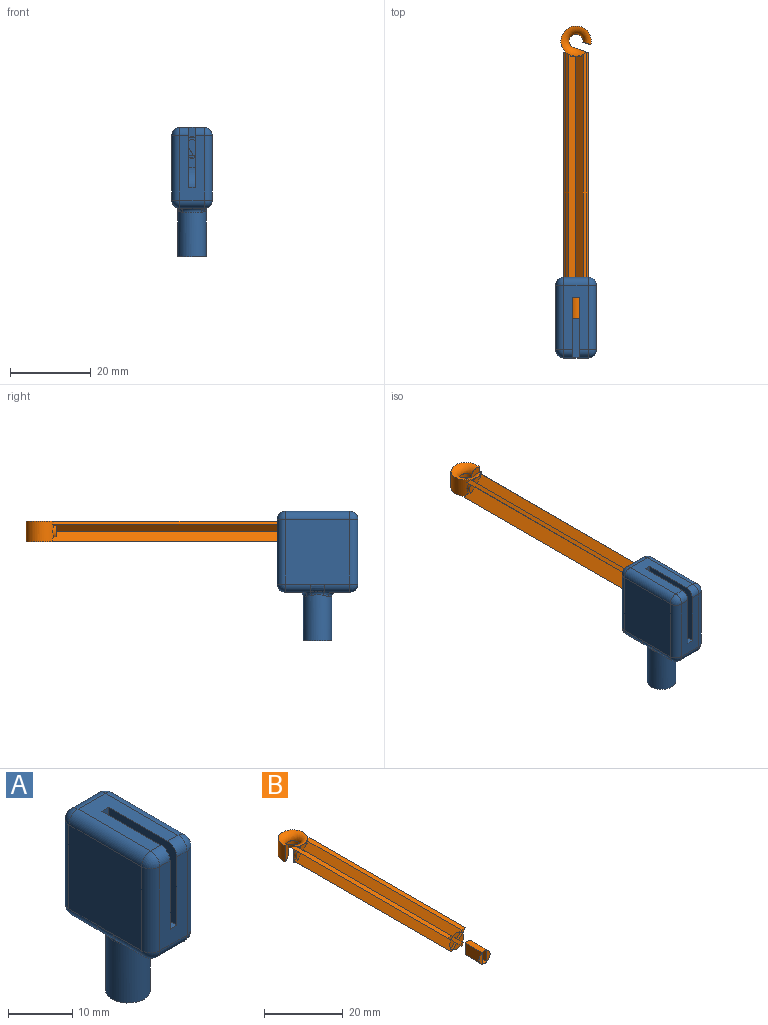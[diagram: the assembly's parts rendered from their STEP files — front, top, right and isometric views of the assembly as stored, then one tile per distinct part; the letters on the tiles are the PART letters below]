
ASSEMBLY  parts=2 mates=1
PART A: 59 faces, bbox 10x33.4x32 mm
  f0: plane 6x4.65mm, normal (0,0,-1), area 23.2mm2, adj f10,f32,f42,f48
  f1: plane 2.34x1.5mm, normal (0,-1,0), area 3.4mm2, adj f15,f16,f17,f56
  f2: cylinder r=2mm len=2.25mm, axis (1,0,0), area 7.1mm2, adj f5,f7,f17,f23
  f3: plane 16x6mm, normal (0,1,0), area 76.4mm2, adj f4,f10,f20,f28,f38
  f4: cylinder r=2mm len=6mm, axis (1,0,0), area 18.8mm2, adj f3,f5,f26,f36
  f5: plane 16x6mm, normal (0,0,1), area 76.5mm2, adj f2,f4,f6,f14,f16,f17,f24,f34
  f6: cylinder r=2mm len=2.25mm, axis (1,0,0), area 7.1mm2, adj f5,f7,f16,f33
  f7: plane 16x6mm, normal (0,-1,0), area 76.5mm2, adj f2,f6,f8,f13,f16,f17,f25,f35
  f8: cylinder r=2mm len=6mm, axis (1,0,0), area 18.8mm2, adj f7,f9,f27,f37
  f9: plane 6x4.65mm, normal (0,0,-1), area 23.2mm2, adj f8,f29,f39,f45
  f10: cylinder r=2mm len=6mm, axis (1,0,0), area 18.8mm2, adj f0,f3,f30,f40
  f11: plane 16.06x16mm, normal (-1,0,0), area 256.1mm2, adj f34,f35,f38,f39,f41,f42
  f12: plane 16.06x16mm, normal (1,0,0), area 256.1mm2, adj f24,f25,f28,f29,f31,f32
  f13: plane 10x1.5mm, normal (0,0,1), area 15mm2, adj f7,f15,f16,f17
  f14: plane 2.34x1.5mm, normal (0,-1,0), area 3.4mm2, adj f5,f16,f17,f53
  f15: cylinder r=5mm len=5mm, axis (1,0,0), area 11.8mm2, adj f1,f13,f16,f17
  f16: plane 15.05x15mm, normal (1,0,0), area 193.8mm2, adj f1,f5,f6,f7,f13,f14,f15,f53
  f17: plane 15.05x15mm, normal (-1,0,0), area 193.8mm2, adj f1,f2,f5,f7,f13,f14,f15,f51
  f18: cylinder r=3.5mm len=11.22mm, axis (0,0,1), area 243.8mm2, adj f19,f43,f44,f45,f46,f47,f48,f49
  f19: plane 7x7mm, normal (0,0,-1), area 38.5mm2, adj f18
  f20: cone r=2.5mm half-angle=3deg, axis (0,1,0), area 184.5mm2, adj f3,f21,f22,f51,f52,f53,f54,f55
  f21: plane 3.06x0.73mm, normal (0,1,0), area 1.5mm2, adj f20,f57
  f22: plane 3.06x0.73mm, normal (0,1,0), area 1.5mm2, adj f20,f52
  f23: sphere r=2mm, area 6.3mm2, adj f2,f24,f25
  f24: cylinder r=2mm len=16mm, axis (0,-1,0), area 50.3mm2, adj f5,f12,f23,f26
  f25: cylinder r=2mm len=16mm, axis (0,0,-1), area 50.3mm2, adj f7,f12,f23,f27
  f26: sphere r=2mm, area 6.3mm2, adj f4,f24,f28
  f27: sphere r=2mm, area 6.3mm2, adj f8,f25,f29
  f28: cylinder r=2mm len=16mm, axis (0,0,1), area 50.3mm2, adj f3,f12,f26,f30
  f29: cylinder r=2mm len=6.2mm, axis (0,1,0), area 18.9mm2, adj f9,f12,f27,f31,f47
  f30: sphere r=2mm, area 6.3mm2, adj f10,f28,f32
  f31: bspline ~5.28x2.45mm, area 7.6mm2, adj f12,f29,f32,f49
  f32: cylinder r=2mm len=6.2mm, axis (0,1,0), area 18.9mm2, adj f0,f12,f30,f31,f50
  f33: sphere r=2mm, area 6.3mm2, adj f6,f34,f35
  f34: cylinder r=2mm len=16mm, axis (0,1,0), area 50.3mm2, adj f5,f11,f33,f36
  f35: cylinder r=2mm len=16mm, axis (0,0,1), area 50.3mm2, adj f7,f11,f33,f37
  f36: sphere r=2mm, area 8.6mm2, adj f4,f34,f38
  f37: sphere r=2mm, area 8.6mm2, adj f8,f35,f39
  f38: cylinder r=2mm len=16mm, axis (0,0,-1), area 50.3mm2, adj f3,f11,f36,f40
  f39: cylinder r=2mm len=6.2mm, axis (0,-1,0), area 18.9mm2, adj f9,f11,f37,f41,f43
  f40: sphere r=2mm, area 4mm2, adj f10,f38,f42
  f41: bspline ~5.28x2.45mm, area 7.6mm2, adj f11,f39,f42,f44
  f42: cylinder r=2mm len=6.2mm, axis (0,-1,0), area 18.9mm2, adj f0,f11,f40,f41,f46
  f43: bspline ~3.1x2.02mm, area 2.2mm2, adj f18,f39,f44,f45
  f44: bspline ~3.88x1.01mm, area 3.5mm2, adj f18,f41,f43,f46
  f45: torus R=4.5mm, axis (0,0,1), area 8.9mm2, adj f9,f18,f43,f47
  f46: bspline ~3.1x2.02mm, area 2.2mm2, adj f18,f42,f44,f48
  f47: bspline ~3.1x2.02mm, area 2.2mm2, adj f18,f29,f45,f49
  f48: torus R=4.5mm, axis (0,0,1), area 8.9mm2, adj f0,f18,f46,f50
  f49: bspline ~3.88x1.01mm, area 3.5mm2, adj f18,f31,f47,f50
  f50: bspline ~2.54x1.89mm, area 2.2mm2, adj f18,f32,f48,f49
  f51: bspline ~25.82x1.92mm, area 3mm2, adj f17,f20,f52,f53
  f52: cylinder r=0.5mm len=4.22mm, axis (0,0,-1), area 2.8mm2, adj f17,f20,f22,f51,f54
  f53: torus R=2.76mm, axis (0,1,0), area 1.4mm2, adj f14,f16,f17,f20,f51,f55
  f54: bspline ~25.82x1.92mm, area 3mm2, adj f17,f20,f52,f56
  f55: bspline ~15.4x1.33mm, area 3mm2, adj f16,f20,f53,f57
  f56: torus R=2.76mm, axis (0,1,0), area 10.2mm2, adj f1,f16,f17,f20,f54,f58
  f57: cylinder r=0.5mm len=4.22mm, axis (0,0,1), area 2.8mm2, adj f16,f20,f21,f55,f58
  f58: bspline ~15.4x1.33mm, area 3mm2, adj f16,f20,f56,f57
PART B: 51 faces, bbox 11.2x74.4x5 mm
  f0: plane 3.57x1.13mm, normal (0,-1,0), area 2.9mm2, adj f41,f49
  f1: plane 56.05x1.41mm, normal (0,0,1), area 79mm2, adj f3,f20,f24,f34,f45
  f2: plane 1.12x1.12mm, normal (0,-1,0), area 0.6mm2, adj f26,f29,f33,f41
  f3: plane 1.83x1.12mm, normal (0,-1,0), area 1.1mm2, adj f1,f20,f34,f41
  f4: plane 1.83x1.12mm, normal (0,-1,0), area 1.1mm2, adj f17,f23,f35,f41
  f5: plane 2.76x1.79mm, normal (0,-1,0), area 2.7mm2, adj f20,f21,f22,f23
  f6: plane 2.76x1.79mm, normal (0,-1,0), area 2.7mm2, adj f29,f30,f31,f32
  f7: plane 2.76x1.79mm, normal (0,-1,0), area 2.7mm2, adj f19,f35,f36
  f8: cylinder r=3.75mm len=1.79mm, axis (0,0,-1), area 0.3mm2, adj f20,f22,f45
  f9: cylinder r=3.75mm len=1.79mm, axis (0,0,-1), area 0.3mm2, adj f21,f23,f45
  f10: cylinder r=3.75mm len=4.39mm, axis (0,0,-1), area 1.6mm2, adj f14,f19,f27,f35,f36,f44
  f11: cylinder r=3.75mm len=1.79mm, axis (0,0,-1), area 0.3mm2, adj f29,f31,f44
  f12: cylinder r=3.75mm len=7.5mm, axis (0,0,-1), area 80.4mm2, adj f16,f18,f24,f26,f33,f34,f44,f45
  f13: cylinder r=1.75mm len=3.5mm, axis (0,0,-1), area 8.5mm2, adj f14,f16,f44,f45
  f14: plane 5x2.6mm, normal (-0.34,0.94,0), area 10.9mm2, adj f10,f13,f25,f44,f45
  f15: cylinder r=3.75mm len=1.79mm, axis (0,0,-1), area 0.3mm2, adj f30,f32,f44
  f16: plane 5.04x1.94mm, normal (0.34,-0.94,0), area 8.4mm2, adj f12,f13,f44,f45
  f17: plane 56.05x1.41mm, normal (0,0,1), area 79mm2, adj f4,f23,f25,f35,f45
  f18: cylinder r=2.5mm len=2.76mm, axis (0,-1,0), area 2.5mm2, adj f12,f28,f33,f34
  f19: cylinder r=2.5mm len=2.76mm, axis (0,-1,0), area 2.5mm2, adj f7,f10,f35,f36
  f20: plane 55.46x1.8mm, normal (-0.71,0,0.71), area 139.7mm2, adj f1,f3,f5,f8,f22,f23,f43
  f21: cylinder r=2.5mm len=1.38mm, axis (0,-1,0), area 0.2mm2, adj f5,f9,f23
  f22: cylinder r=2.5mm len=1.38mm, axis (0,-1,0), area 0.2mm2, adj f5,f8,f20
  f23: plane 55.46x1.8mm, normal (0.71,0,0.71), area 139.7mm2, adj f4,f5,f9,f17,f20,f21,f43
  f24: plane 0.61x0.61mm, normal (0,1,0), area 0.2mm2, adj f1,f12,f34
  f25: plane 0.61x0.61mm, normal (0,1,0), area 0.2mm2, adj f14,f17,f35
  f26: plane 55.98x0.74mm, normal (0.71,0,-0.71), area 55.7mm2, adj f2,f12,f29,f33
  f27: plane 55.98x0.74mm, normal (-0.71,0,-0.71), area 55.7mm2, adj f10,f30,f36,f37
  f28: plane 2.76x1.79mm, normal (0,-1,0), area 2.7mm2, adj f18,f33,f34
  f29: plane 55.46x1.8mm, normal (-0.71,0,-0.71), area 139.7mm2, adj f2,f6,f11,f26,f30,f31,f38
  f30: plane 55.46x1.8mm, normal (0.71,0,-0.71), area 139.7mm2, adj f6,f15,f27,f29,f32,f37,f38
  f31: cylinder r=2.5mm len=1.38mm, axis (0,-1,0), area 0.2mm2, adj f6,f11,f29
  f32: cylinder r=2.5mm len=1.38mm, axis (0,-1,0), area 0.2mm2, adj f6,f15,f30
  f33: plane 55.97x1.8mm, normal (0.71,0,0.71), area 139.9mm2, adj f2,f12,f18,f26,f28,f34,f39
  f34: plane 56.07x2.52mm, normal (0.71,0,-0.71), area 196mm2, adj f1,f3,f12,f18,f24,f28,f33,f39
  f35: plane 56.07x2.52mm, normal (-0.71,0,-0.71), area 196mm2, adj f4,f7,f10,f17,f19,f25,f36,f40
  f36: plane 55.97x1.8mm, normal (-0.71,0,0.71), area 139.9mm2, adj f7,f10,f19,f27,f35,f37,f40
  f37: plane 1.12x1.12mm, normal (0,-1,0), area 0.6mm2, adj f27,f30,f36,f41
  f38: plane 2.76x1.79mm, normal (0,1,0), area 2.7mm2, adj f29,f30,f41
  f39: plane 2.76x1.79mm, normal (0,1,0), area 2.7mm2, adj f33,f34,f41
  f40: plane 2.76x1.79mm, normal (0,1,0), area 2.7mm2, adj f35,f36,f41
  f41: cone r=2.5mm half-angle=3deg, axis (0,1,0), area 140.8mm2, adj f0,f2,f3,f4,f37,f38,f39,f40
  f42: plane 3.57x1.13mm, normal (0,-1,0), area 2.9mm2, adj f41,f47
  f43: plane 2.76x1.79mm, normal (0,1,0), area 2.7mm2, adj f20,f23,f41
  f44: torus R=3.75mm, axis (0,0,1), area 41.9mm2, adj f10,f11,f12,f13,f14,f15,f16
  f45: torus R=3.75mm, axis (0,0,1), area 41.9mm2, adj f1,f8,f9,f12,f13,f14,f16,f17
  f46: cylinder r=1.98mm len=6mm, axis (0,-1,0), area 10.5mm2, adj f41,f47,f49,f50
  f47: plane 6x3.57mm, normal (-1,0,0), area 21.4mm2, adj f42,f46,f48,f50
  f48: cylinder r=1.98mm len=6mm, axis (0,-1,0), area 10.5mm2, adj f41,f47,f49,f50
  f49: plane 6x3.57mm, normal (1,0,0), area 21.4mm2, adj f0,f46,f48,f50
  f50: plane 3.95x1.7mm, normal (0,-1,0), area 6.5mm2, adj f46,f47,f48,f49
PLACE A t=(4.45,23.15,-10.59)mm
PLACE B rot(axis=(0,1,0),180deg) t=(-0.55,81.6,4.41)mm
MATE slider A.f20 <-> B.f41  axis (0,1,0) through (-0.55,18.09,4.41)mm
